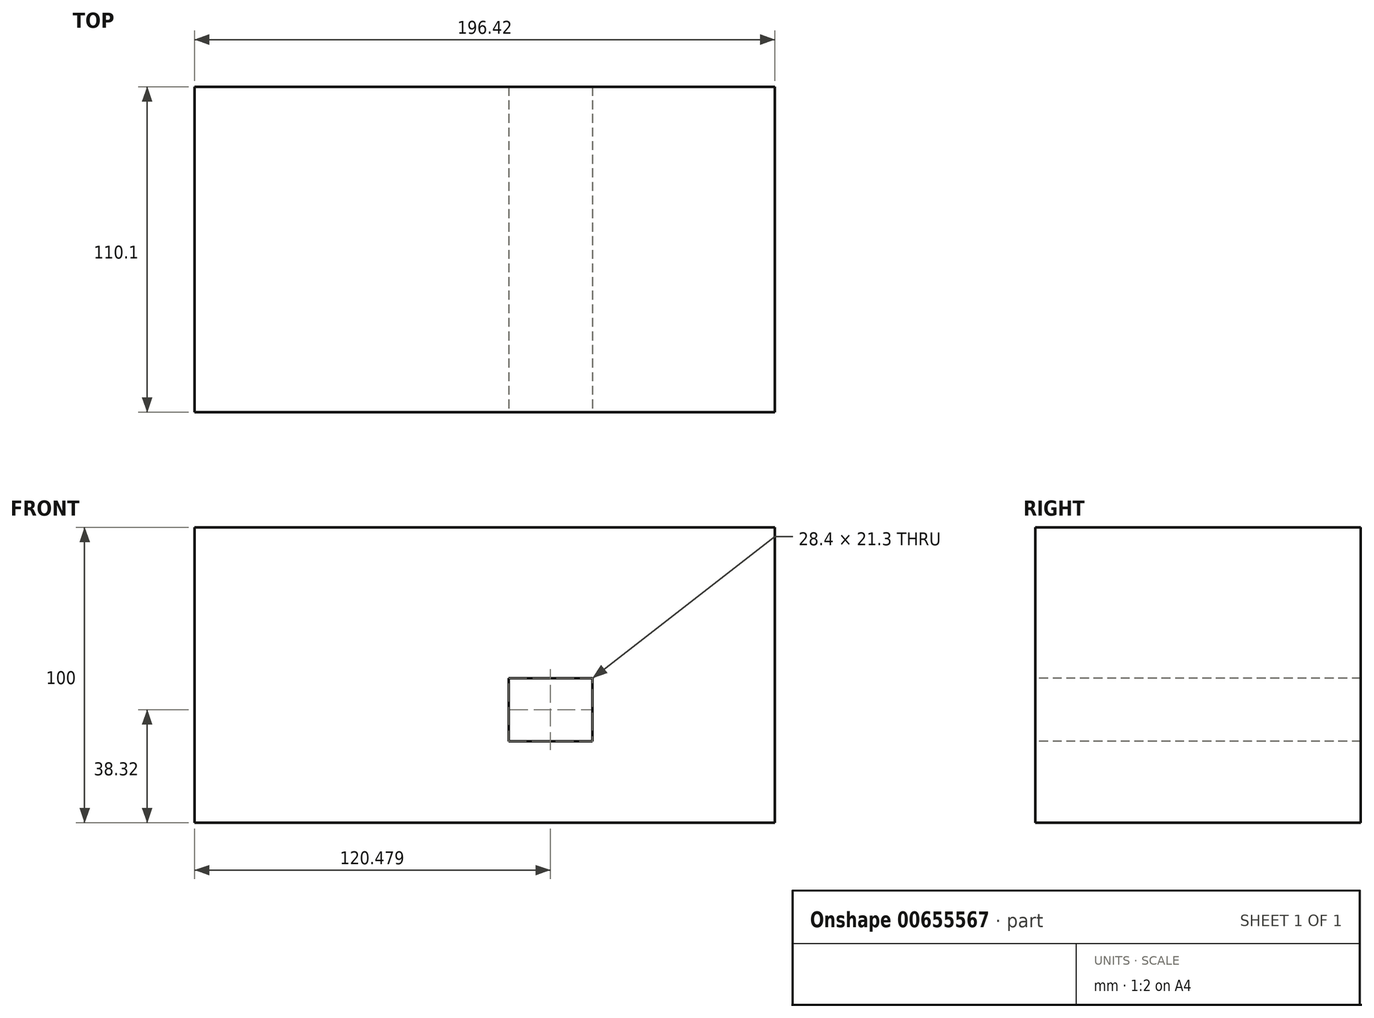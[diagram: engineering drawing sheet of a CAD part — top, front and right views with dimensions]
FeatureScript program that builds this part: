
annotation { "Feature Type Name" : "Feature", "Feature Type Description" : "" }
export const myFeature = defineFeature(function(context is Context, id is Id, definition is map)
    precondition{}
    {
        {
            var Q0;
            Q0=qCreatedBy(makeId("Top.planeOp"),FACE);
            var sketch = newSketch(context, id + "F0", { "sketchPlane" : qUnion([Q0])});
            skLineSegment(sketch, "E0.bottom", {"start": v(98.2, 55.05) * mm, "end": v(-98.2, 55.05) * mm});
            skLineSegment(sketch, "E0.top", {"start": v(98.2, -55.05) * mm, "end": v(-98.2, -55.05) * mm});
            skLineSegment(sketch, "E0.left", {"start": v(98.2, 55.05) * mm, "end": v(98.2, -55.05) * mm});
            skLineSegment(sketch, "E0.right", {"start": v(-98.2, 55.05) * mm, "end": v(-98.2, -55.05) * mm});
            skPoint(sketch, "E0.middle", {"position": v(0, 0) * mm});
            skLineSegment(sketch, "E1.bottom", {"start": v(0, 0) * mm, "end": v(42.33, 0) * mm});
            skLineSegment(sketch, "E1.top", {"start": v(0, 21.12) * mm, "end": v(42.33, 21.12) * mm});
            skLineSegment(sketch, "E1.left", {"start": v(0, 0) * mm, "end": v(0, 21.12) * mm});
            skLineSegment(sketch, "E1.right", {"start": v(42.33, 0) * mm, "end": v(42.33, 21.12) * mm});
            skSolve(sketch);
        }
        {
            var Q0;
            Q0=makeQuery(id+"F0.imprint","IMPRINT",FACE,{"disambiguationData":[TD([[makeQuery(id+"F0.imprint","IMPRINT",EDGE,{"derivedFrom":sQuery(id+"F0.wireOp",EDGE,"E0.bottom")}),1.0]])]});
            var Q1;
            Q1=makeQuery(id+"F0.imprint","IMPRINT",FACE,{"disambiguationData":[TD([[makeQuery(id+"F0.imprint","IMPRINT",EDGE,{"derivedFrom":sQuery(id+"F0.wireOp",EDGE,"E1.bottom")}),1.0]])]});
            extrude(context, id + "F1", {"entities" : qUnion([Q0, Q1]), "depth" : 100 * mm, "offsetDistance" : 25 * mm});
        }
        {
            var Q0;
            Q0=qCreatedBy(makeId("Front.planeOp"),FACE);
            var sketch = newSketch(context, id + "F2", { "sketchPlane" : qUnion([Q0])});
            skLineSegment(sketch, "E2.bottom", {"start": v(36.47, 27.67) * mm, "end": v(8.07, 27.67) * mm});
            skLineSegment(sketch, "E2.top", {"start": v(36.47, 48.97) * mm, "end": v(8.07, 48.97) * mm});
            skLineSegment(sketch, "E2.left", {"start": v(36.47, 27.67) * mm, "end": v(36.47, 48.97) * mm});
            skLineSegment(sketch, "E2.right", {"start": v(8.07, 27.67) * mm, "end": v(8.07, 48.97) * mm});
            skSolve(sketch);
        }
        {
            var Q0;
            Q0=makeQuery(id+"F2.imprint","IMPRINT",FACE,{"disambiguationData":[TD([[makeQuery(id+"F2.imprint","IMPRINT",EDGE,{"derivedFrom":sQuery(id+"F2.wireOp",EDGE,"E2.bottom")}),-1.0]])]});
            extrude(context, id + "F3", {"entities" : qUnion([Q0]), "operationType" : NewBodyOperationType.REMOVE, "endBound" : BoundingType.THROUGH_ALL, "oppositeDirection" : true, "depth" : 25 * mm, "offsetDistance" : 25 * mm, "hasSecondDirection" : true, "secondDirectionBound" : SecondDirectionBoundingType.THROUGH_ALL, "secondDirectionOppositeDirection" : false, "secondDirectionDepth" : 25 * mm});
        }
    });
